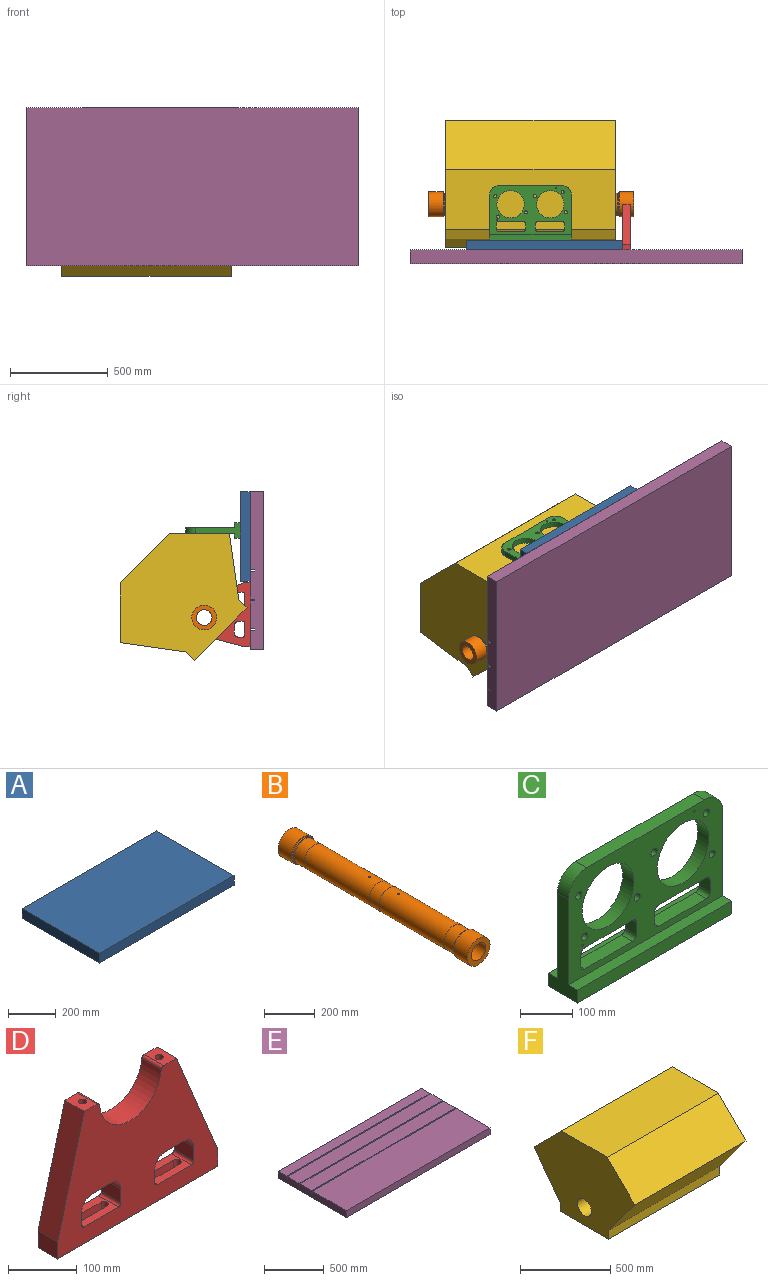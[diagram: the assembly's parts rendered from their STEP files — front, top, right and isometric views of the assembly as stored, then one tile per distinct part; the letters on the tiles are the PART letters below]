
ASSEMBLY  parts=6 mates=9
PART A: 6 faces, bbox 800x460x50 mm
  f0: plane 800x50mm, normal (0,1,0), area 40000mm2, adj f1,f3,f4,f5
  f1: plane 460x50mm, normal (-1,0,0), area 23000mm2, adj f0,f2,f4,f5
  f2: plane 800x50mm, normal (0,-1,0), area 40000mm2, adj f1,f3,f4,f5
  f3: plane 460x50mm, normal (1,0,0), area 23000mm2, adj f0,f2,f4,f5
  f4: plane 800x460mm, normal (0,0,1), area 368000mm2, adj f0,f1,f2,f3
  f5: plane 800x460mm, normal (0,0,-1), area 368000mm2, adj f0,f1,f2,f3
PART B: 24 faces, bbox 132.8x1050x132.8 mm
  f0: cylinder r=56.2mm len=112.4mm, axis (0,-1,0), area 1589mm2, adj f4,f6
  f1: plane 127x127mm, normal (0,1,0), area 1657.5mm2, adj f3,f4
  f2: plane 127x127mm, normal (0,-1,0), area 7641.1mm2, adj f3,f23
  f3: cylinder r=63.5mm len=127mm, axis (0,1,0), area 29923.7mm2, adj f1,f2
  f4: torus R=59.2mm, axis (0,-1,0), area 1696.3mm2, adj f0,f1
  f5: cylinder r=56.1mm len=112.2mm, axis (0,1,0), area 19386.8mm2, adj f6,f7
  f6: plane 112.4x112.4mm, normal (0,1,0), area 35.3mm2, adj f0,f5
  f7: plane 112.4x112.4mm, normal (0,-1,0), area 35.3mm2, adj f5,f9
  f8: cylinder r=4mm len=16.4mm, axis (0,0,-1), area 407.9mm2, adj f9,f23
  f9: cylinder r=56.2mm len=360mm, axis (0,-1,0), area 127070.9mm2, adj f7,f8,f11
  f10: cylinder r=56.1mm len=112.2mm, axis (0,1,0), area 19386.8mm2, adj f11,f12
  f11: plane 112.4x112.4mm, normal (0,1,0), area 35.3mm2, adj f9,f10
  f12: plane 112.4x112.4mm, normal (0,-1,0), area 35.3mm2, adj f10,f14
  f13: cylinder r=4mm len=16.4mm, axis (0,0,-1), area 407.9mm2, adj f14,f23
  f14: cylinder r=56.2mm len=360mm, axis (0,-1,0), area 127070.9mm2, adj f12,f13,f16
  f15: cylinder r=56.1mm len=112.2mm, axis (0,1,0), area 19386.8mm2, adj f16,f17
  f16: plane 112.4x112.4mm, normal (0,1,0), area 35.3mm2, adj f14,f15
  f17: plane 112.4x112.4mm, normal (0,-1,0), area 35.3mm2, adj f15,f22
  f18: plane 127x127mm, normal (0,1,0), area 7641.1mm2, adj f19,f23
  f19: cylinder r=63.5mm len=127mm, axis (0,1,0), area 29923.7mm2, adj f18,f20
  f20: plane 127x127mm, normal (0,-1,0), area 1657.5mm2, adj f19,f21
  f21: torus R=59.2mm, axis (0,-1,0), area 1696.3mm2, adj f20,f22
  f22: cylinder r=56.2mm len=112.4mm, axis (0,-1,0), area 1589mm2, adj f17,f21
  f23: cylinder r=40mm len=1050mm, axis (0,-1,0), area 263792.9mm2, adj f2,f8,f13,f18
PART C: 42 faces, bbox 418.5x80x280 mm
  f0: plane 418.5x250mm, normal (0,1,0), area 56552.6mm2, adj f4,f5,f7,f8,f9,f10,f11,f12
  f1: plane 418.5x250mm, normal (0,-1,0), area 56613.8mm2, adj f2,f3,f4,f5,f7,f8,f9,f10
  f2: cylinder r=2.5mm len=15mm, axis (0,-1,0), area 235.6mm2, adj f1,f19
  f3: cylinder r=2.5mm len=15mm, axis (0,-1,0), area 235.6mm2, adj f1,f17
  f4: plane 318.5x30mm, normal (0,0,1), area 9555mm2, adj f0,f1,f40,f41
  f5: plane 230x80mm, normal (-1,0,0), area 8400mm2, adj f0,f1,f6,f20,f21,f22,f23,f40
  f6: plane 418.5x80mm, normal (0,0,-1), area 33480mm2, adj f5,f7,f21,f23
  f7: plane 230x80mm, normal (1,0,0), area 8400mm2, adj f0,f1,f6,f20,f21,f22,f23,f41
  f8: cylinder r=70mm len=140mm, axis (0,-1,0), area 13194.7mm2, adj f0,f1
  f9: cylinder r=8.25mm len=30mm, axis (0,-1,0), area 1555.1mm2, adj f0,f1
  f10: cylinder r=8.25mm len=30mm, axis (0,-1,0), area 1555.1mm2, adj f0,f1
  f11: cylinder r=8.25mm len=30mm, axis (0,-1,0), area 1555.1mm2, adj f0,f1
  f12: cylinder r=70mm len=140mm, axis (0,-1,0), area 13194.7mm2, adj f0,f1
  f13: cylinder r=8.25mm len=30mm, axis (0,-1,0), area 1555.1mm2, adj f0,f1
  f14: cylinder r=8.25mm len=30mm, axis (0,-1,0), area 1555.1mm2, adj f0,f1
  f15: cylinder r=8.25mm len=30mm, axis (0,-1,0), area 1555.1mm2, adj f0,f1
  f16: cylinder r=4mm len=15mm, axis (0,1,0), area 377mm2, adj f0,f17
  f17: plane 8x8mm, normal (0,1,0), area 30.6mm2, adj f3,f16
  f18: cylinder r=4mm len=15mm, axis (0,1,0), area 377mm2, adj f0,f19
  f19: plane 8x8mm, normal (0,1,0), area 30.6mm2, adj f2,f18
  f20: plane 418.5x25mm, normal (0,0,1), area 10462.5mm2, adj f1,f5,f7,f21
  f21: plane 418.5x30mm, normal (0,-1,0), area 12555mm2, adj f5,f6,f7,f20
  f22: plane 418.5x25mm, normal (0,0,1), area 10462.5mm2, adj f0,f5,f7,f23
  f23: plane 418.5x30mm, normal (0,1,0), area 12555mm2, adj f5,f6,f7,f22
  f24: plane 130x30mm, normal (0,0,-1), area 3900mm2, adj f0,f1,f32,f35
  f25: plane 30x30mm, normal (1,0,0), area 900mm2, adj f0,f1,f32,f33
  f26: plane 130x30mm, normal (0,0,1), area 3900mm2, adj f0,f1,f33,f34
  f27: plane 30x30mm, normal (-1,0,0), area 900mm2, adj f0,f1,f34,f35
  f28: plane 130x30mm, normal (0,0,-1), area 3900mm2, adj f0,f1,f36,f39
  f29: plane 30x30mm, normal (1,0,0), area 900mm2, adj f0,f1,f38,f39
  f30: plane 130x30mm, normal (0,0,1), area 3900mm2, adj f0,f1,f37,f38
  f31: plane 30x30mm, normal (-1,0,0), area 900mm2, adj f0,f1,f36,f37
  f32: cylinder r=10mm len=30mm, axis (0,1,0), area 471.2mm2, adj f0,f1,f24,f25
  f33: cylinder r=10mm len=30mm, axis (0,1,0), area 471.2mm2, adj f0,f1,f25,f26
  f34: cylinder r=10mm len=30mm, axis (0,1,0), area 471.2mm2, adj f0,f1,f26,f27
  f35: cylinder r=10mm len=30mm, axis (0,1,0), area 471.2mm2, adj f0,f1,f24,f27
  f36: cylinder r=10mm len=30mm, axis (0,1,0), area 471.2mm2, adj f0,f1,f28,f31
  f37: cylinder r=10mm len=30mm, axis (0,1,0), area 471.2mm2, adj f0,f1,f30,f31
  f38: cylinder r=10mm len=30mm, axis (0,1,0), area 471.2mm2, adj f0,f1,f29,f30
  f39: cylinder r=10mm len=30mm, axis (0,1,0), area 471.2mm2, adj f0,f1,f28,f29
  f40: cylinder r=50mm len=50mm, axis (0,1,0), area 2356.2mm2, adj f0,f1,f4,f5
  f41: cylinder r=50mm len=50mm, axis (0,1,0), area 2356.2mm2, adj f0,f1,f4,f7
PART D: 40 faces, bbox 330x40x235 mm
  f0: plane 330x40mm, normal (0,0,-1), area 11667.1mm2, adj f6,f7,f16,f17,f30,f31,f32,f33
  f1: plane 70x40mm, normal (0,0,1), area 2033.5mm2, adj f16,f17,f20,f21,f32,f33,f34,f35
  f2: plane 70x40mm, normal (0,0,1), area 2033.5mm2, adj f16,f17,f18,f19,f30,f31,f36,f37
  f3: cylinder r=63.5mm len=126.66mm, axis (0,1,0), area 7608.5mm2, adj f16,f17,f38,f39
  f4: plane 40x26.68mm, normal (0,0,1), area 954.2mm2, adj f5,f16,f17,f29,f38
  f5: plane 205x55mm, normal (-0.97,0,0.26), area 8490mm2, adj f4,f6,f16,f17
  f6: plane 40x30mm, normal (-1,0,0), area 1200mm2, adj f0,f5,f16,f17
  f7: plane 40x30mm, normal (1,0,0), area 1200mm2, adj f0,f8,f16,f17
  f8: plane 205x85mm, normal (0.92,0,0.38), area 8876.9mm2, adj f7,f15,f16,f17
  f9: plane 40x25mm, normal (1,0,0), area 1000mm2, adj f16,f17,f21,f24
  f10: plane 40x40mm, normal (0,0,-1), area 1600mm2, adj f16,f17,f24,f25
  f11: plane 40x25mm, normal (-1,0,0), area 1000mm2, adj f16,f17,f20,f25
  f12: plane 40x25mm, normal (1,0,0), area 1000mm2, adj f16,f17,f19,f22
  f13: plane 40x40mm, normal (0,0,-1), area 1600mm2, adj f16,f17,f22,f23
  f14: plane 40x25mm, normal (-1,0,0), area 1000mm2, adj f16,f17,f18,f23
  f15: plane 40x26.68mm, normal (0,0,1), area 954.2mm2, adj f8,f16,f17,f27,f39
  f16: plane 330x235mm, normal (0,-1,0), area 49221.4mm2, adj f0,f1,f2,f3,f4,f5,f6,f7
  f17: plane 330x235mm, normal (0,1,0), area 49221.4mm2, adj f0,f1,f2,f3,f4,f5,f6,f7
  f18: cylinder r=5mm len=40mm, axis (0,-1,0), area 314.2mm2, adj f2,f14,f16,f17
  f19: cylinder r=5mm len=40mm, axis (0,-1,0), area 314.2mm2, adj f2,f12,f16,f17
  f20: cylinder r=5mm len=40mm, axis (0,-1,0), area 314.2mm2, adj f1,f11,f16,f17
  f21: cylinder r=5mm len=40mm, axis (0,-1,0), area 314.2mm2, adj f1,f9,f16,f17
  f22: cylinder r=20mm len=40mm, axis (0,-1,0), area 1256.6mm2, adj f12,f13,f16,f17
  f23: cylinder r=20mm len=40mm, axis (0,-1,0), area 1256.6mm2, adj f13,f14,f16,f17
  f24: cylinder r=20mm len=40mm, axis (0,-1,0), area 1256.6mm2, adj f9,f10,f16,f17
  f25: cylinder r=20mm len=40mm, axis (0,-1,0), area 1256.6mm2, adj f10,f11,f16,f17
  f26: cone r=0mm half-angle=59deg, axis (0,0,1), area 131.9mm2, adj f27
  f27: cylinder r=6mm len=40mm, axis (0,0,1), area 1508mm2, adj f15,f26
  f28: cone r=0mm half-angle=59deg, axis (0,0,1), area 131.9mm2, adj f29
  f29: cylinder r=6mm len=40mm, axis (0,0,1), area 1508mm2, adj f4,f28
  f30: plane 51.5x30mm, normal (0,1,0), area 1545mm2, adj f0,f2,f36,f37
  f31: plane 51.5x30mm, normal (0,-1,0), area 1545mm2, adj f0,f2,f36,f37
  f32: plane 51.5x30mm, normal (0,1,0), area 1545mm2, adj f0,f1,f34,f35
  f33: plane 51.5x30mm, normal (0,-1,0), area 1545mm2, adj f0,f1,f34,f35
  f34: cylinder r=6.25mm len=30mm, axis (0,0,1), area 589mm2, adj f0,f1,f32,f33
  f35: cylinder r=6.25mm len=30mm, axis (0,0,1), area 589mm2, adj f0,f1,f32,f33
  f36: cylinder r=6.25mm len=30mm, axis (0,0,1), area 589mm2, adj f0,f2,f30,f31
  f37: cylinder r=6.25mm len=30mm, axis (0,0,1), area 589mm2, adj f0,f2,f30,f31
  f38: cylinder r=5mm len=40mm, axis (0,1,0), area 299.5mm2, adj f3,f4,f16,f17
  f39: cylinder r=5mm len=40mm, axis (0,1,0), area 299.5mm2, adj f3,f15,f16,f17
PART E: 18 faces, bbox 1700x810x70 mm
  f0: plane 1700x100mm, normal (0,0,1), area 170000mm2, adj f4,f5,f6,f15
  f1: plane 1700x140mm, normal (0,0,1), area 238000mm2, adj f4,f5,f12,f16
  f2: plane 1700x140mm, normal (0,0,1), area 238000mm2, adj f4,f5,f9,f13
  f3: plane 1700x400mm, normal (0,0,1), area 680000mm2, adj f4,f5,f7,f10
  f4: plane 810x70mm, normal (-1,0,0), area 55950mm2, adj f0,f1,f2,f3,f6,f7,f8,f9
  f5: plane 810x70mm, normal (1,0,0), area 55950mm2, adj f0,f1,f2,f3,f6,f7,f8,f9
  f6: plane 1700x70mm, normal (0,1,0), area 119000mm2, adj f0,f4,f5,f8
  f7: plane 1700x70mm, normal (0,-1,0), area 119000mm2, adj f3,f4,f5,f8
  f8: plane 1700x810mm, normal (0,0,-1), area 1377000mm2, adj f4,f5,f6,f7
  f9: plane 1700x25mm, normal (0,-1,0), area 42500mm2, adj f2,f4,f5,f11
  f10: plane 1700x25mm, normal (0,1,0), area 42500mm2, adj f3,f4,f5,f11
  f11: plane 1700x10mm, normal (0,0,1), area 17000mm2, adj f4,f5,f9,f10
  f12: plane 1700x25mm, normal (0,-1,0), area 42500mm2, adj f1,f4,f5,f14
  f13: plane 1700x25mm, normal (0,1,0), area 42500mm2, adj f2,f4,f5,f14
  f14: plane 1700x10mm, normal (0,0,1), area 17000mm2, adj f4,f5,f12,f13
  f15: plane 1700x25mm, normal (0,-1,0), area 42500mm2, adj f0,f4,f5,f17
  f16: plane 1700x25mm, normal (0,1,0), area 42500mm2, adj f1,f4,f5,f17
  f17: plane 1700x10mm, normal (0,0,1), area 17000mm2, adj f4,f5,f15,f16
PART F: 11 faces, bbox 870x790x550 mm
  f0: plane 870x60mm, normal (0,-1,0), area 52200mm2, adj f1,f7,f8,f9
  f1: plane 870x380mm, normal (0,0,-1), area 330600mm2, adj f0,f2,f8,f9
  f2: plane 870x60mm, normal (0,1,0), area 52200mm2, adj f1,f3,f8,f9
  f3: plane 870x273.33mm, normal (0,0.8,-0.6), area 297250mm2, adj f2,f4,f8,f9
  f4: plane 870x216.67mm, normal (0,0.71,0.71), area 266579.3mm2, adj f3,f5,f8,f9
  f5: plane 870x356.67mm, normal (0,0,1), area 310300mm2, adj f4,f6,f8,f9
  f6: plane 870x216.67mm, normal (0,-0.71,0.71), area 266579.3mm2, adj f5,f7,f8,f9
  f7: plane 870x273.33mm, normal (0,-0.8,-0.6), area 297250mm2, adj f0,f6,f8,f9
  f8: plane 790x550mm, normal (1,0,0), area 297418.9mm2, adj f0,f1,f2,f3,f4,f5,f6,f7
  f9: plane 790x550mm, normal (-1,0,0), area 297418.9mm2, adj f0,f1,f2,f3,f4,f5,f6,f7
  f10: cylinder r=55mm len=870mm, axis (-1,0,0), area 300650.4mm2, adj f8,f9
PLACE A rot(axis=(-1,0,0),90deg) t=(-1721.46,-463.45,231.66)mm
PLACE B rot(axis=(0,0,1),90deg) t=(-1775.81,-228.45,-198.55)mm
PLACE C rot(axis=(-1,0,0),90deg) t=(-1779.35,-413.45,231.61)mm
PLACE D rot(axis=(-0.58,-0.58,-0.58),120deg) t=(-1268.31,-463.45,-348.55)mm
PLACE E rot(axis=(-1,0,0),90deg) t=(-1549.73,-533.45,-31.97)mm
PLACE F rot(axis=(-1,0,0),45deg) t=(-2214.31,-313.31,-283.4)mm
MATE planar C.f0 <-> F.f6  axis (0,0,-1) through (-1779.31,-254.77,231.61)mm
MATE planar A.f2 <-> E.f7  axis (0,0,1) through (-1708.31,-438.45,446.45)mm
MATE planar D.f0 <-> E.f1  axis (0,-1,0) through (-1288.31,-463.45,-183.55)mm
MATE planar D.f16 <-> A.f3  axis (-1,0,0) through (-1308.31,-362.13,-189.01)mm
MATE revolute B.f3 <-> D.f3  axis (-1,0,0) through (-1288.31,-228.45,-198.55)mm
MATE cylindrical F.f10 <-> D.f3  axis (-1,0,0) through (-1344.31,-228.45,-198.55)mm
MATE planar A.f5 <-> E.f3  axis (0,-1,0) through (-2108.31,-463.45,216.45)mm
MATE planar C.f6 <-> A.f4  axis (0,-1,0) through (-1779.35,-413.45,246.61)mm
MATE parallel F.f4 <-> A.f4  axis (0,1,0) through (-1779.31,201.7,-173.8)mm
